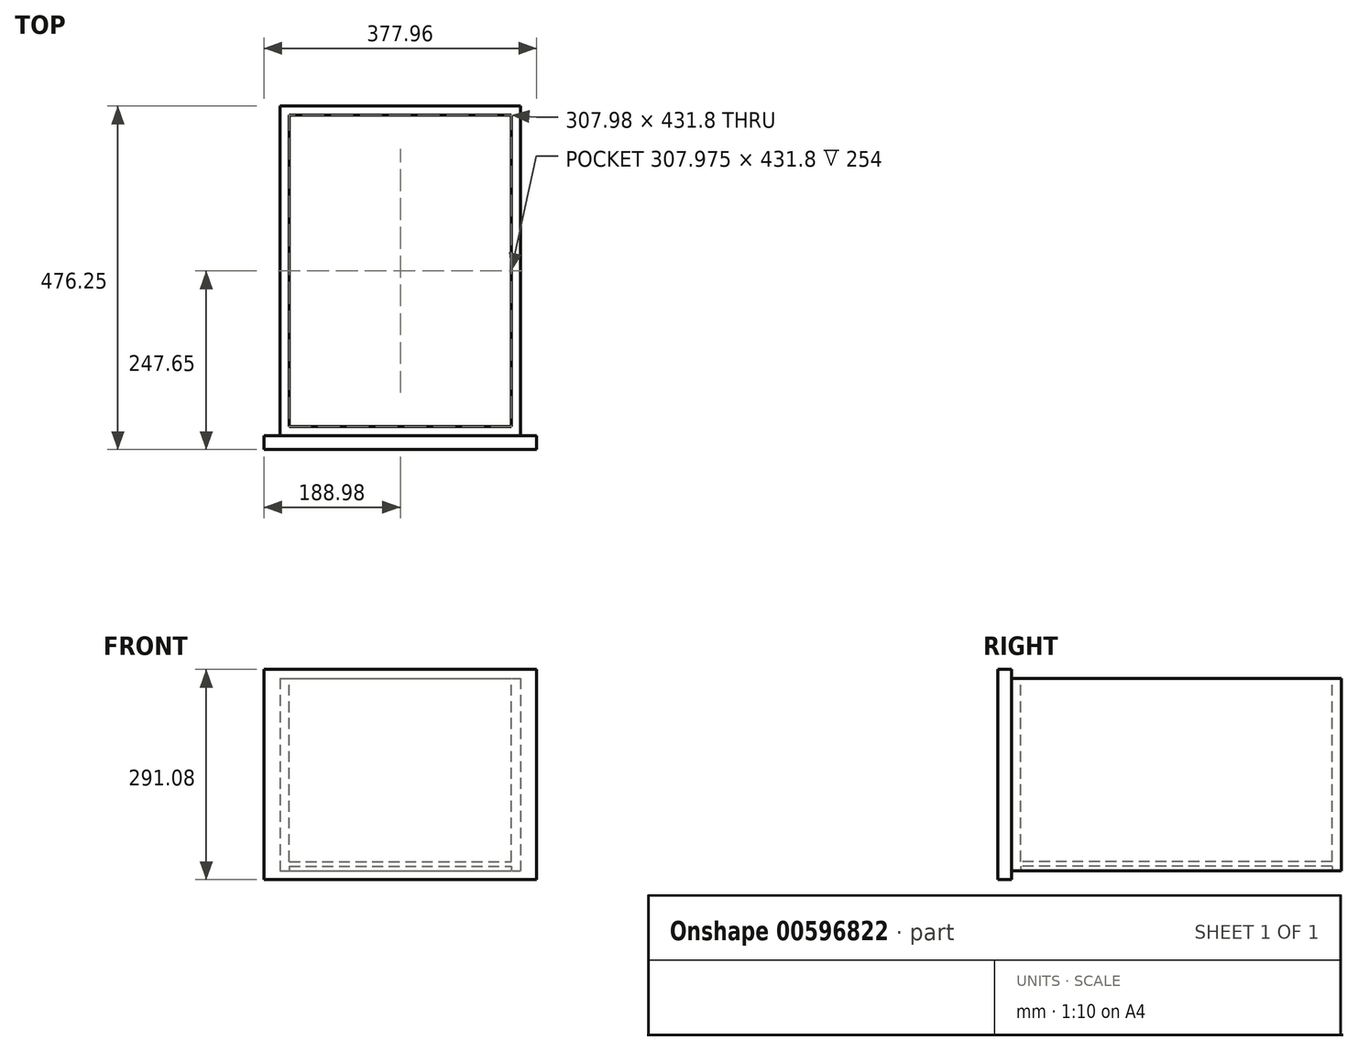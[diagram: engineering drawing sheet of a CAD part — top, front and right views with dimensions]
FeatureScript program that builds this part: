
annotation { "Feature Type Name" : "Feature", "Feature Type Description" : "" }
export const myFeature = defineFeature(function(context is Context, id is Id, definition is map)
    precondition{}
    {
        {
            var Q0;
            Q0=qCreatedBy(makeId("Front.planeOp"),FACE);
            var sketch = newSketch(context, id + "F0", { "sketchPlane" : qUnion([Q0])});
            skLineSegment(sketch, "E0.bottom", {"start": v(-188.98, 145.54) * mm, "end": v(188.98, 145.54) * mm});
            skLineSegment(sketch, "E0.top", {"start": v(-188.98, -145.54) * mm, "end": v(188.98, -145.54) * mm});
            skLineSegment(sketch, "E0.left", {"start": v(-188.98, 145.54) * mm, "end": v(-188.98, -145.54) * mm});
            skLineSegment(sketch, "E0.right", {"start": v(188.98, 145.54) * mm, "end": v(188.98, -145.54) * mm});
            skPoint(sketch, "E0.middle", {"position": v(0, 0) * mm});
            skSolve(sketch);
        }
        {
            var Q0;
            Q0=makeQuery(id+"F0.imprint","IMPRINT",FACE,{"disambiguationData":[TD([[makeQuery(id+"F0.imprint","IMPRINT",EDGE,{"derivedFrom":sQuery(id+"F0.wireOp",EDGE,"E0.bottom")}),-1.0]])]});
            extrude(context, id + "F1", {"entities" : qUnion([Q0]), "depth" : 19.05 * mm, "offsetDistance" : 25.4 * mm});
        }
        {
            var Q0;
            Q0=makeQuery(id+"F1.opExtrude","CAP_FACE",FACE,{"disambiguationData":[OSD([sQuery(id+"F0.wireOp",EDGE,"E0.bottom"),sQuery(id+"F0.wireOp",EDGE,"E0.top"),sQuery(id+"F0.wireOp",EDGE,"E0.left"),sQuery(id+"F0.wireOp",EDGE,"E0.right")])],"isStart":true});
            var sketch = newSketch(context, id + "F2", { "sketchPlane" : qUnion([Q0])});
            skLineSegment(sketch, "E1.bottom", {"start": v(166.69, 133.35) * mm, "end": v(-166.69, 133.35) * mm});
            skLineSegment(sketch, "E1.top", {"start": v(166.69, -133.35) * mm, "end": v(-166.69, -133.35) * mm});
            skLineSegment(sketch, "E1.left", {"start": v(166.69, 133.35) * mm, "end": v(166.69, -133.35) * mm});
            skLineSegment(sketch, "E1.right", {"start": v(-166.69, 133.35) * mm, "end": v(-166.69, -133.35) * mm});
            skPoint(sketch, "E1.middle", {"position": v(0, 0) * mm});
            skSolve(sketch);
        }
        {
            var Q0;
            Q0=makeQuery(id+"F2.imprint","IMPRINT",FACE,{"disambiguationData":[TD([[makeQuery(id+"F2.imprint","IMPRINT",EDGE,{"derivedFrom":sQuery(id+"F2.wireOp",EDGE,"E1.bottom")}),1.0]])]});
            extrude(context, id + "F3", {"entities" : qUnion([Q0]), "operationType" : NewBodyOperationType.ADD, "depth" : 457.2 * mm, "offsetDistance" : 25.4 * mm});
        }
        {
            var Q0;
            Q0=makeQuery(id+"F3.opExtrude","SWEPT_FACE",FACE,{"disambiguationData":[OSD([sQuery(id+"F2.wireOp",EDGE,"E1.bottom")])]});
            var sketch = newSketch(context, id + "F4", { "sketchPlane" : qUnion([Q0])});
            skLineSegment(sketch, "E2.bottom", {"start": v(-153.99, 444.5) * mm, "end": v(153.99, 444.5) * mm});
            skLineSegment(sketch, "E2.top", {"start": v(-153.99, 12.7) * mm, "end": v(153.99, 12.7) * mm});
            skLineSegment(sketch, "E2.left", {"start": v(-153.99, 444.5) * mm, "end": v(-153.99, 12.7) * mm});
            skLineSegment(sketch, "E2.right", {"start": v(153.99, 444.5) * mm, "end": v(153.99, 12.7) * mm});
            skPoint(sketch, "E2.middle", {"position": v(0, 228.6) * mm});
            skPoint(sketch, "E2.middle.positionSnap0", {"position": v(-166.69, 228.6) * mm});
            skPoint(sketch, "E2.centerSnap0", {"position": v(-166.69, 228.6) * mm});
            skSolve(sketch);
        }
        {
            var Q0;
            Q0=makeQuery(id+"F4.imprint","IMPRINT",FACE,{"disambiguationData":[TD([[makeQuery(id+"F4.imprint","IMPRINT",EDGE,{"derivedFrom":sQuery(id+"F4.wireOp",EDGE,"E2.bottom")}),-1.0]])]});
            extrude(context, id + "F5", {"entities" : qUnion([Q0]), "operationType" : NewBodyOperationType.REMOVE, "oppositeDirection" : true, "depth" : 254 * mm, "offsetDistance" : 25.4 * mm});
        }
        {
            var Q0;
            Q0=makeQuery(id+"F3.opExtrude","SWEPT_FACE",FACE,{"disambiguationData":[OSD([sQuery(id+"F2.wireOp",EDGE,"E1.top")])]});
            var sketch = newSketch(context, id + "F6", { "sketchPlane" : qUnion([Q0])});
            skLineSegment(sketch, "E3.bottom", {"start": v(-153.99, -444.5) * mm, "end": v(153.99, -444.5) * mm});
            skLineSegment(sketch, "E3.top", {"start": v(-153.99, -12.7) * mm, "end": v(153.99, -12.7) * mm});
            skLineSegment(sketch, "E3.left", {"start": v(-153.99, -444.5) * mm, "end": v(-153.99, -12.7) * mm});
            skLineSegment(sketch, "E3.right", {"start": v(153.99, -444.5) * mm, "end": v(153.99, -12.7) * mm});
            skPoint(sketch, "E3.middle", {"position": v(0, -228.6) * mm});
            skPoint(sketch, "E3.middle.positionSnap0", {"position": v(166.69, -228.6) * mm});
            skPoint(sketch, "E3.centerSnap0", {"position": v(166.69, -228.6) * mm});
            skSolve(sketch);
        }
        {
            var Q0;
            Q0=makeQuery(id+"F6.imprint","IMPRINT",FACE,{"disambiguationData":[TD([[makeQuery(id+"F6.imprint","IMPRINT",EDGE,{"derivedFrom":sQuery(id+"F6.wireOp",EDGE,"E3.bottom")}),1.0]])]});
            extrude(context, id + "F7", {"entities" : qUnion([Q0]), "operationType" : NewBodyOperationType.REMOVE, "oppositeDirection" : true, "depth" : 6.35 * mm, "offsetDistance" : 25.4 * mm});
        }
    });
